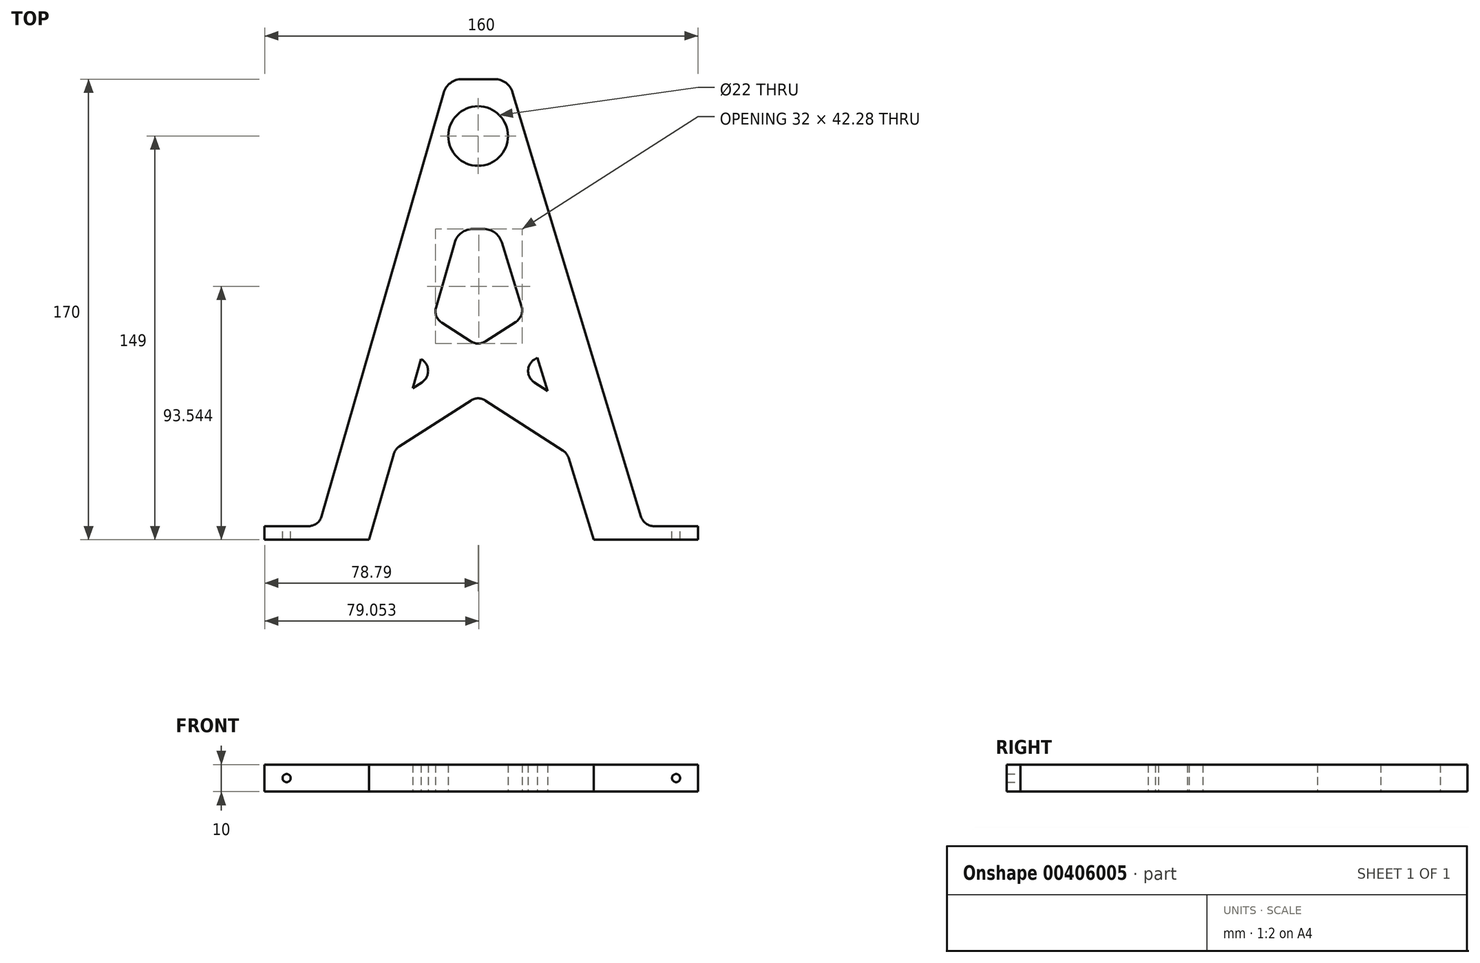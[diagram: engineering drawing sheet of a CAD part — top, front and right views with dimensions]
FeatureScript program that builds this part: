
annotation { "Feature Type Name" : "Feature", "Feature Type Description" : "" }
export const myFeature = defineFeature(function(context is Context, id is Id, definition is map)
    precondition{}
    {
        {
            var Q0;
            Q0=qCreatedBy(makeId("Top.planeOp"),FACE);
            var sketch = newSketch(context, id + "F0", { "sketchPlane" : qUnion([Q0])});
            skLineSegment(sketch, "E0", {"start": v(0, 0) * mm, "end": v(0, 170) * mm, "construction": true});
            skCircle(sketch, "E1", {"center": v(0, 149) * mm, "radius": 11 * mm});
            skLineSegment(sketch, "E2", {"start": v(6.07, 170) * mm, "end": v(-6, 170) * mm});
            skLineSegment(sketch, "E3", {"start": v(-12.73, 164.94) * mm, "end": v(-57.75, 8.62) * mm});
            skLineSegment(sketch, "E4", {"start": v(12.77, 165.03) * mm, "end": v(60.13, 8.55) * mm});
            skLineSegment(sketch, "E5", {"start": v(-60.23, 0) * mm, "end": v(-40.23, 0) * mm});
            skLineSegment(sketch, "E6", {"start": v(-40.23, 0) * mm, "end": v(-31.14, 31.59) * mm});
            skLineSegment(sketch, "E7", {"start": v(-1.93, 114.68) * mm, "end": v(2.04, 114.68) * mm});
            skLineSegment(sketch, "E8", {"start": v(8.73, 109.76) * mm, "end": v(16.04, 86.14) * mm});
            skLineSegment(sketch, "E9", {"start": v(42.72, 0) * mm, "end": v(62.72, 0) * mm});
            skPoint(sketch, "E10.visualSharp", {"position": v(-7.2, 114.68) * mm});
            skArc(sketch, "E10.filletArc", {"start": v(-1.93, 114.68) * mm, "mid": v(-6.14, 113.28) * mm, "end": v(-8.66, 109.62) * mm});
            skPoint(sketch, "E11.visualSharp", {"position": v(7.2, 114.68) * mm});
            skArc(sketch, "E11.filletArc", {"start": v(8.73, 109.76) * mm, "mid": v(6.2, 113.32) * mm, "end": v(2.04, 114.68) * mm});
            skLineSegment(sketch, "E12", {"start": v(-7.2, 114.68) * mm, "end": v(0, 0) * mm, "construction": true});
            skLineSegment(sketch, "E13", {"start": v(7.2, 114.68) * mm, "end": v(0, 0) * mm, "construction": true});
            skPoint(sketch, "E14.visualSharp", {"position": v(-11.27, 170) * mm});
            skArc(sketch, "E14.filletArc", {"start": v(-6, 170) * mm, "mid": v(-10.2, 168.6) * mm, "end": v(-12.73, 164.94) * mm});
            skPoint(sketch, "E15.visualSharp", {"position": v(11.27, 170) * mm});
            skArc(sketch, "E15.filletArc", {"start": v(12.77, 165.03) * mm, "mid": v(10.25, 168.62) * mm, "end": v(6.07, 170) * mm});
            skLineSegment(sketch, "E16", {"start": v(-24.13, 55.9) * mm, "end": v(-20.75, 58.09) * mm});
            skLineSegment(sketch, "E17", {"start": v(25.72, 54.88) * mm, "end": v(20.75, 58.09) * mm});
            skLineSegment(sketch, "E18", {"start": v(-29.04, 34.4) * mm, "end": v(-2.7, 51.37) * mm});
            skLineSegment(sketch, "E19", {"start": v(31.29, 32.95) * mm, "end": v(2.7, 51.37) * mm});
            skLineSegment(sketch, "E20.trimOffspring", {"start": v(-2.7, 73.2) * mm, "end": v(-13.45, 80.12) * mm});
            skLineSegment(sketch, "E21.trimOffspring", {"start": v(2.7, 73.2) * mm, "end": v(13.97, 80.46) * mm});
            skLineSegment(sketch, "E22.trimOffspring", {"start": v(20.75, 66.5) * mm, "end": v(21.9, 67.23) * mm});
            skLineSegment(sketch, "E23.trimOffspring", {"start": v(-20.75, 66.5) * mm, "end": v(-21.03, 66.67) * mm});
            skLineSegment(sketch, "E24", {"start": v(0, 71.46) * mm, "end": v(0, 53.12) * mm, "construction": true});
            skLineSegment(sketch, "E25", {"start": v(-14.23, 62.29) * mm, "end": v(14.23, 62.29) * mm, "construction": true});
            skLineSegment(sketch, "E26", {"start": v(-14.23, 62.29) * mm, "end": v(0, 0) * mm, "construction": true});
            skLineSegment(sketch, "E27", {"start": v(14.23, 62.29) * mm, "end": v(0, 0) * mm, "construction": true});
            skLineSegment(sketch, "E28.trimOffspring", {"start": v(-15.55, 85.71) * mm, "end": v(-8.66, 109.62) * mm});
            skLineSegment(sketch, "E29.trimOffspring", {"start": v(-24.13, 55.9) * mm, "end": v(-21.03, 66.67) * mm});
            skLineSegment(sketch, "E30.trimOffspring", {"start": v(21.9, 67.23) * mm, "end": v(25.72, 54.88) * mm});
            skLineSegment(sketch, "E31.trimOffspring", {"start": v(33.36, 30.23) * mm, "end": v(42.72, 0) * mm});
            skPoint(sketch, "E32.visualSharp", {"position": v(0, 71.46) * mm});
            skArc(sketch, "E32.filletArc", {"start": v(-2.7, 73.2) * mm, "mid": v(0, 72.4) * mm, "end": v(2.7, 73.2) * mm});
            skPoint(sketch, "E33.visualSharp", {"position": v(0, 53.12) * mm});
            skArc(sketch, "E33.filletArc", {"start": v(2.7, 51.37) * mm, "mid": v(0, 52.17) * mm, "end": v(-2.7, 51.37) * mm});
            skPoint(sketch, "E34.visualSharp", {"position": v(14.23, 62.29) * mm});
            skArc(sketch, "E34.filletArc", {"start": v(20.75, 66.5) * mm, "mid": v(18.46, 62.29) * mm, "end": v(20.75, 58.09) * mm});
            skPoint(sketch, "E35.visualSharp", {"position": v(-14.23, 62.29) * mm});
            skArc(sketch, "E35.filletArc", {"start": v(-20.75, 58.09) * mm, "mid": v(-18.46, 62.29) * mm, "end": v(-20.75, 66.5) * mm});
            skPoint(sketch, "E36.visualSharp", {"position": v(-16.57, 82.14) * mm});
            skArc(sketch, "E36.filletArc", {"start": v(-15.55, 85.71) * mm, "mid": v(-15.42, 82.57) * mm, "end": v(-13.45, 80.12) * mm});
            skPoint(sketch, "E37.visualSharp", {"position": v(17.16, 82.52) * mm});
            skArc(sketch, "E37.filletArc", {"start": v(13.97, 80.46) * mm, "mid": v(15.96, 82.95) * mm, "end": v(16.04, 86.14) * mm});
            skPoint(sketch, "E38.visualSharp", {"position": v(32.82, 31.97) * mm});
            skArc(sketch, "E38.filletArc", {"start": v(33.36, 30.23) * mm, "mid": v(32.56, 31.77) * mm, "end": v(31.29, 32.95) * mm});
            skPoint(sketch, "E39.visualSharp", {"position": v(-30.62, 33.39) * mm});
            skArc(sketch, "E39.filletArc", {"start": v(-29.04, 34.4) * mm, "mid": v(-30.34, 33.18) * mm, "end": v(-31.14, 31.59) * mm});
            skLineSegment(sketch, "E40", {"start": v(-62.56, 5) * mm, "end": v(-78.8, 5) * mm});
            skLineSegment(sketch, "E41", {"start": v(-78.8, 5) * mm, "end": v(-78.8, 0) * mm});
            skLineSegment(sketch, "E42", {"start": v(-78.8, 0) * mm, "end": v(-60.23, 0) * mm});
            skLineSegment(sketch, "E43", {"start": v(64.92, 5) * mm, "end": v(81.2, 5) * mm});
            skLineSegment(sketch, "E44", {"start": v(81.2, 5) * mm, "end": v(81.2, 0) * mm});
            skLineSegment(sketch, "E45", {"start": v(81.2, 0) * mm, "end": v(62.72, 0) * mm});
            skPoint(sketch, "E46.visualSharp", {"position": v(-58.8, 5) * mm});
            skArc(sketch, "E46.filletArc", {"start": v(-62.56, 5) * mm, "mid": v(-59.55, 6) * mm, "end": v(-57.75, 8.62) * mm});
            skPoint(sketch, "E47.visualSharp", {"position": v(61.2, 5) * mm});
            skArc(sketch, "E47.filletArc", {"start": v(60.13, 8.55) * mm, "mid": v(61.94, 5.98) * mm, "end": v(64.92, 5) * mm});
            skSolve(sketch);
        }
        {
            var Q0;
            Q0=makeQuery(id+"F0.imprint","IMPRINT",FACE,{"disambiguationData":[TD([[makeQuery(id+"F0.imprint","IMPRINT",EDGE,{"derivedFrom":sQuery(id+"F0.wireOp",EDGE,"E1")}),-1.0]])]});
            extrude(context, id + "F1", {"entities" : qUnion([Q0]), "depth" : 10 * mm});
        }
        {
            var Q0;
            Q0=makeQuery(id+"F1.opExtrude","SWEPT_FACE",FACE,{"disambiguationData":[OSD([sQuery(id+"F0.wireOp",EDGE,"E40")])]});
            var sketch = newSketch(context, id + "F2", { "sketchPlane" : qUnion([Q0])});
            skLineSegment(sketch, "E48", {"start": v(62.56, 10) * mm, "end": v(78.8, 0) * mm, "construction": true});
            skLineSegment(sketch, "E49", {"start": v(62.56, 0) * mm, "end": v(78.8, 10) * mm, "construction": true});
            skCircle(sketch, "E50", {"center": v(70.67, 5) * mm, "radius": 1.5 * mm});
            skLineSegment(sketch, "E51", {"start": v(0, 51.62) * mm, "end": v(0, -21.63) * mm, "construction": true});
            skSolve(sketch);
        }
        {
            var Q0;
            Q0=makeQuery(id+"F1.opExtrude","SWEPT_FACE",FACE,{"disambiguationData":[OSD([sQuery(id+"F0.wireOp",EDGE,"E43")])]});
            var sketch = newSketch(context, id + "F3", { "sketchPlane" : qUnion([Q0])});
            skLineSegment(sketch, "E52", {"start": v(-81.2, 10) * mm, "end": v(-64.92, 0) * mm, "construction": true});
            skCircle(sketch, "E53", {"center": v(-73.06, 5) * mm, "radius": 1.5 * mm});
            skSolve(sketch);
        }
        {
            var Q0;
            Q0=makeQuery(id+"F3.imprint","IMPRINT",FACE,{"disambiguationData":[TD([[makeQuery(id+"F3.imprint","IMPRINT",EDGE,{"derivedFrom":sQuery(id+"F3.wireOp",EDGE,"E53")}),1.0]])]});
            var Q1;
            Q1=makeQuery(id+"F2.imprint","IMPRINT",FACE,{"disambiguationData":[TD([[makeQuery(id+"F2.imprint","IMPRINT",EDGE,{"derivedFrom":sQuery(id+"F2.wireOp",EDGE,"E50")}),1.0]])]});
            extrude(context, id + "F4", {"entities" : qUnion([Q0, Q1]), "operationType" : NewBodyOperationType.REMOVE, "oppositeDirection" : true, "depth" : 25 * mm});
        }
    });
